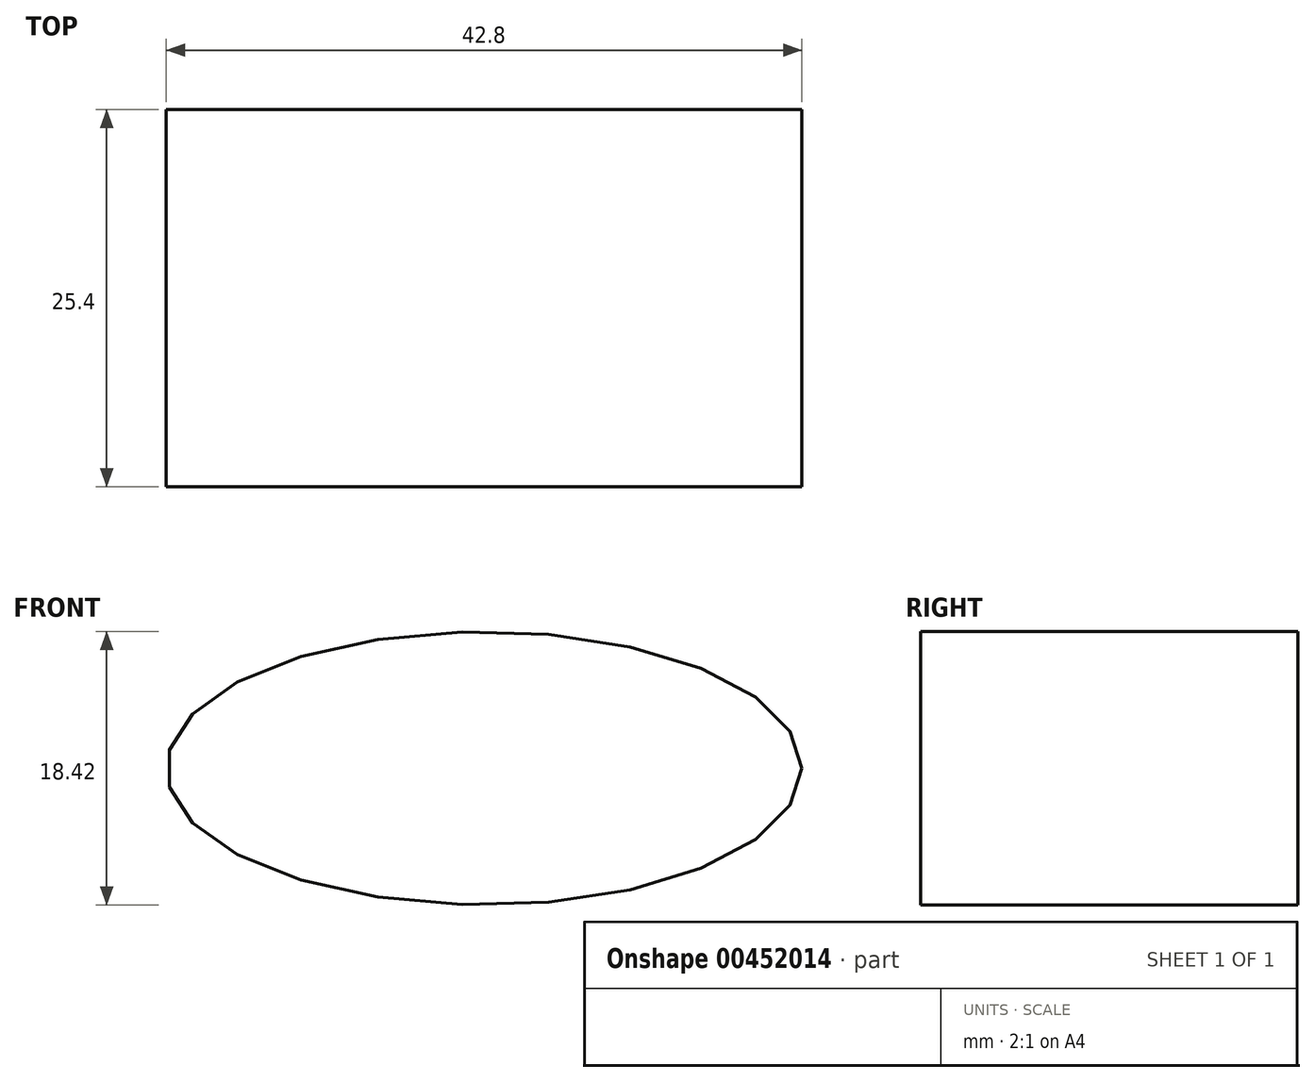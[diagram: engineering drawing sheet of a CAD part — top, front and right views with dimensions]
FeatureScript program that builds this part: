
annotation { "Feature Type Name" : "Feature", "Feature Type Description" : "" }
export const myFeature = defineFeature(function(context is Context, id is Id, definition is map)
    precondition{}
    {
        {
            var Q0;
            Q0=qCreatedBy(makeId("Front.planeOp"),FACE);
            var sketch = newSketch(context, id + "F0", { "sketchPlane" : qUnion([Q0])});
            skEllipse(sketch, "E0", {"center": v(0, 0) * mm, "majorRadius": 21.4 * mm, "minorRadius": 9.2 * mm, "majorAxis": v(1, 0)});
            skSolve(sketch);
        }
        {
            var Q0;
            Q0 = qSketchRegion(id + "F0", true);
            extrude(context, id + "F1", {"entities" : qUnion([Q0]), "depth" : 25.4 * mm});
        }
    });
